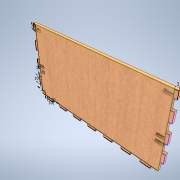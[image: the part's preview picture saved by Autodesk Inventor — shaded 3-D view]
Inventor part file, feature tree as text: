
AUTODESK INVENTOR PART (.ipt)
format: ipt  version: 2021 (Build 250183000, 183)  size: 234,496 bytes
history: native  units: mm
features: extrude x3, sketch x3
ambient origin geometry x8: Origin, YZ Plane, XZ Plane, XY Plane, X Axis, Y Axis, Z Axis, Center Point
bodies: Solid1 (feature_tree)
feature tree (6):
  extrude  "Extrusion1"  Depth=77.0mm
  extrude  "Extrusion2"  Depth=3.0mm
  extrude  "Extrusion3"  Depth=30.0mm
  sketch  "Sketch1"  dims[d0=99.0mm d1=77.0mm]
  sketch  "Sketch2"  dims[d2=3.0mm d3=0.0mm d13=3.0mm]
  sketch  "Sketch3"  dims[d14=10.0mm d15=30.0mm d17=20.0mm d18=10.0mm d20=10.0mm d22=3.0mm d23=7.0mm d24=3.0mm d25=3.0mm d26=0.0mm d27=7.0mm d28=3.0mm d29=20.0mm d31=92.0mm d32=20.0mm d34=38.0mm d37=0.0mm d38=0.0mm d39=20.0mm d41=6.0mm d42=20.0mm d44=92.0mm d47=3.1mm d48=13.0mm d49=5.75mm d50=17.5mm d51=17.5mm d52=17.5mm d53=17.5mm d54=17.5mm d55=5.75mm]
